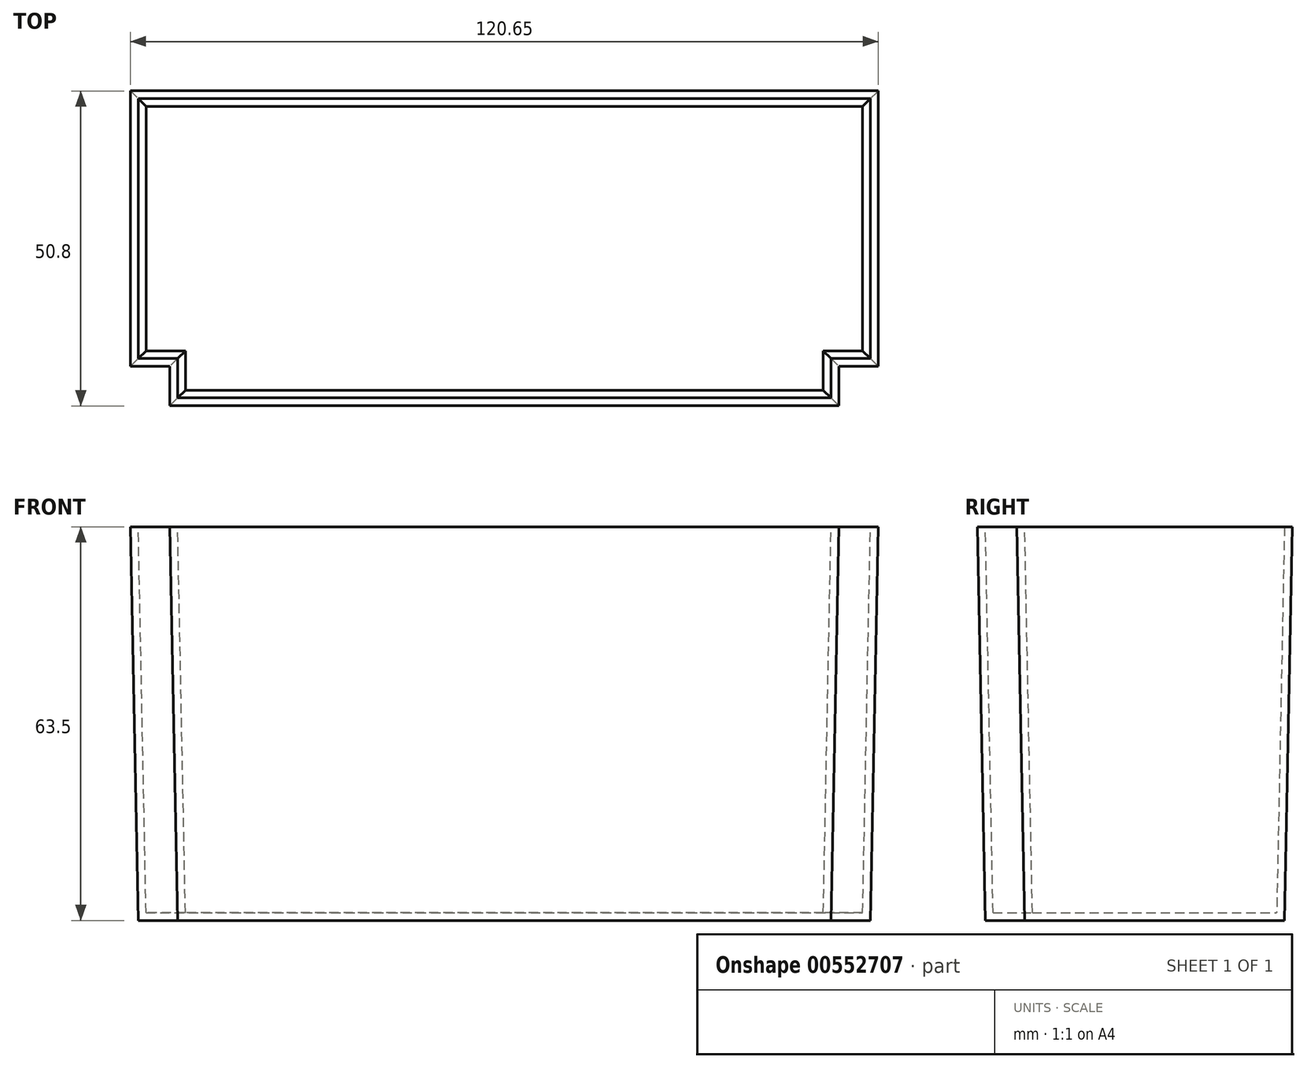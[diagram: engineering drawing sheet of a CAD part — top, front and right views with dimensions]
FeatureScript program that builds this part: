
annotation { "Feature Type Name" : "Feature", "Feature Type Description" : "" }
export const myFeature = defineFeature(function(context is Context, id is Id, definition is map)
    precondition{}
    {
        {
            var Q0;
            Q0=qCreatedBy(makeId("Top.planeOp"),FACE);
            var sketch = newSketch(context, id + "F0", { "sketchPlane" : qUnion([Q0])});
            skLineSegment(sketch, "E0", {"start": v(-51.65, 34.01) * mm, "end": v(69, 34.01) * mm});
            skLineSegment(sketch, "E1", {"start": v(69, 34.01) * mm, "end": v(69, -10.44) * mm});
            skLineSegment(sketch, "E2", {"start": v(69, -10.44) * mm, "end": v(62.65, -10.44) * mm});
            skLineSegment(sketch, "E3", {"start": v(62.65, -10.44) * mm, "end": v(62.65, -16.79) * mm});
            skLineSegment(sketch, "E4", {"start": v(62.65, -16.79) * mm, "end": v(-45.3, -16.79) * mm});
            skLineSegment(sketch, "E5", {"start": v(-45.3, -16.79) * mm, "end": v(-45.3, -10.44) * mm});
            skLineSegment(sketch, "E6", {"start": v(-45.3, -10.44) * mm, "end": v(-51.65, -10.44) * mm});
            skLineSegment(sketch, "E7", {"start": v(-51.65, -10.44) * mm, "end": v(-51.65, 34.01) * mm});
            skLineSegment(sketch, "E8", {"start": v(-50.38, 32.74) * mm, "end": v(67.73, 32.74) * mm});
            skLineSegment(sketch, "E9", {"start": v(67.73, 32.74) * mm, "end": v(67.73, -9.17) * mm});
            skLineSegment(sketch, "E10", {"start": v(67.73, -9.17) * mm, "end": v(61.38, -9.17) * mm});
            skLineSegment(sketch, "E11", {"start": v(61.38, -9.17) * mm, "end": v(61.38, -15.52) * mm});
            skLineSegment(sketch, "E12", {"start": v(61.38, -15.52) * mm, "end": v(-44.03, -15.52) * mm});
            skLineSegment(sketch, "E13", {"start": v(-44.03, -15.52) * mm, "end": v(-44.03, -9.17) * mm});
            skLineSegment(sketch, "E14", {"start": v(-44.03, -9.17) * mm, "end": v(-50.38, -9.17) * mm});
            skLineSegment(sketch, "E15", {"start": v(-50.38, -9.17) * mm, "end": v(-50.38, 32.74) * mm});
            skCircle(sketch, "E16", {"center": v(46.97, 21.17) * mm, "radius": 8.45 * mm});
            skSolve(sketch);
        }
        {
            var Q0;
            Q0 = qSketchRegion(id + "F0", true);
            var Q1;
            Q1=makeQuery(id+"F0.imprint","IMPRINT",FACE,{"disambiguationData":[TD([[makeQuery(id+"F0.imprint","IMPRINT",EDGE,{"derivedFrom":sQuery(id+"F0.wireOp",EDGE,"E8")}),-1.0]])]});
            var Q2;
            Q2=makeQuery(id+"F0.imprint","IMPRINT",FACE,{"disambiguationData":[TD([[makeQuery(id+"F0.imprint","IMPRINT",EDGE,{"derivedFrom":sQuery(id+"F0.wireOp",EDGE,"E16")}),1.0]])]});
            extrude(context, id + "F1", {"entities" : qUnion([Q0, Q1, Q2]), "depth" : 63.5 * mm, "offsetDistance" : 25.4 * mm});
        }
        {
            var Q0;
            Q0=makeQuery(id+"F1.opExtrude","CAP_EDGE",EDGE,{"disambiguationData":[OSD([sQuery(id+"F0.wireOp",EDGE,"E7")])],"isStart":true});
            chamfer(context, id + "F2", {"entities" : qUnion([Q0]), "chamferType" : ChamferType.TWO_OFFSETS, "width1" : 1.27 * mm, "oppositeDirection" : false, "width2" : 63.5 * mm, "tangentPropagation" : true});
        }
        {
            var Q0;
            Q0=makeQuery(id+"F1.opExtrude","CAP_EDGE",EDGE,{"disambiguationData":[OSD([sQuery(id+"F0.wireOp",EDGE,"E6")])],"isStart":true});
            chamfer(context, id + "F3", {"entities" : qUnion([Q0]), "chamferType" : ChamferType.TWO_OFFSETS, "width1" : 1.27 * mm, "oppositeDirection" : false, "width2" : 63.5 * mm, "tangentPropagation" : true});
        }
        {
            var Q0;
            Q0=makeQuery(id+"F1.opExtrude","CAP_EDGE",EDGE,{"disambiguationData":[OSD([sQuery(id+"F0.wireOp",EDGE,"E5")])],"isStart":true});
            chamfer(context, id + "F4", {"entities" : qUnion([Q0]), "chamferType" : ChamferType.TWO_OFFSETS, "width1" : 1.27 * mm, "oppositeDirection" : false, "width2" : 63.5 * mm, "tangentPropagation" : true});
        }
        {
            var Q0;
            Q0=makeQuery(id+"F1.opExtrude","CAP_EDGE",EDGE,{"disambiguationData":[OSD([sQuery(id+"F0.wireOp",EDGE,"E4")])],"isStart":true});
            chamfer(context, id + "F5", {"entities" : qUnion([Q0]), "chamferType" : ChamferType.TWO_OFFSETS, "width1" : 1.27 * mm, "oppositeDirection" : false, "width2" : 63.5 * mm, "tangentPropagation" : true});
        }
        {
            var Q0;
            Q0=makeQuery(id+"F1.opExtrude","CAP_EDGE",EDGE,{"disambiguationData":[OSD([sQuery(id+"F0.wireOp",EDGE,"E3")])],"isStart":true});
            chamfer(context, id + "F6", {"entities" : qUnion([Q0]), "chamferType" : ChamferType.TWO_OFFSETS, "width1" : 1.27 * mm, "oppositeDirection" : false, "width2" : 63.5 * mm, "tangentPropagation" : true});
        }
        {
            var Q0;
            Q0=makeQuery(id+"F1.opExtrude","CAP_EDGE",EDGE,{"disambiguationData":[OSD([sQuery(id+"F0.wireOp",EDGE,"E2")])],"isStart":true});
            chamfer(context, id + "F7", {"entities" : qUnion([Q0]), "chamferType" : ChamferType.TWO_OFFSETS, "width1" : 1.27 * mm, "oppositeDirection" : false, "width2" : 63.5 * mm, "tangentPropagation" : true});
        }
        {
            var Q0;
            Q0=makeQuery(id+"F1.opExtrude","CAP_EDGE",EDGE,{"disambiguationData":[OSD([sQuery(id+"F0.wireOp",EDGE,"E1")])],"isStart":true});
            chamfer(context, id + "F8", {"entities" : qUnion([Q0]), "chamferType" : ChamferType.TWO_OFFSETS, "width1" : 1.27 * mm, "oppositeDirection" : false, "width2" : 63.5 * mm, "tangentPropagation" : true});
        }
        {
            var Q0;
            Q0=makeQuery(id+"F1.opExtrude","CAP_EDGE",EDGE,{"disambiguationData":[OSD([sQuery(id+"F0.wireOp",EDGE,"E0")])],"isStart":true});
            chamfer(context, id + "F9", {"entities" : qUnion([Q0]), "chamferType" : ChamferType.TWO_OFFSETS, "width1" : 1.27 * mm, "oppositeDirection" : false, "width2" : 63.5 * mm, "tangentPropagation" : true});
        }
        {
            var Q0;
            Q0=makeQuery(id+"F1.opExtrude","CAP_FACE",FACE,{"disambiguationData":[OSD([sQuery(id+"F0.wireOp",EDGE,"E0"),sQuery(id+"F0.wireOp",EDGE,"E1"),sQuery(id+"F0.wireOp",EDGE,"E2"),sQuery(id+"F0.wireOp",EDGE,"E3"),sQuery(id+"F0.wireOp",EDGE,"E4"),sQuery(id+"F0.wireOp",EDGE,"E5"),sQuery(id+"F0.wireOp",EDGE,"E6"),sQuery(id+"F0.wireOp",EDGE,"E7")])],"isStart":false});
            shell(context, id + "F10", {"entities" : qUnion([Q0]), "thickness" : 1.27 * mm});
        }
    });
